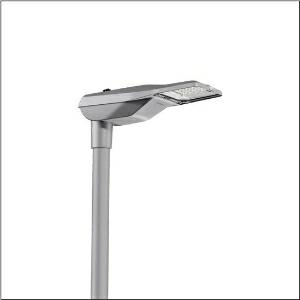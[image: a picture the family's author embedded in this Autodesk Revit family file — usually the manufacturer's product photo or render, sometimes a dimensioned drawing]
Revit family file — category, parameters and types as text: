
# Revit family: streetlight_sl_21_iq_micro___p0_5a_5xe1v31v08db_2d7c
name_source: partatom
category: Lighting Fixtures
units: mm (PartAtom-declared; Revit-internal decimal feet)

## family parameters
Cut with Voids When Loaded = No
Host = Face
Light Source = No
Part Type = Normal
Room Calculation Point = No
Round Connector Dimension = Use Diameter
Shared = No

## types (1)
- --- (1 x LED, 5030 lm, 39.1 W, 3000K)
    Apparent Load = 39 VA
    CIE Flux Codes = 37 73 96 100 100
    Color Rendering = 70
    Color Temperature = 3000K
    Default Elevation = 1800 mm
    Description = Streetlight SL 21 iQ micro, mast luminaire, primary light control with lens, of PMMA, primary optical cover: cover, of toughened safety glass, transparent, light distribution: P0.5a, light emission: direct distribution, primary light characteristic: asymmetric, installation type: post-top, side-entry, LED, High Power LED, rated luminous flux: 5.030lm, luminous efficacy: 129lm/W, light colour: 730, colour temperature: 3000K, control gear: iQ-Street Remote, D4i with power reduction, control: pre-setting: logarithmic dimming characteristic, Street-Remote, Auto-Match, Temp-Guard, Lumen-Switch, Night-Set, Smart-Wire, Light-Fading, Desk-Remote (wireless, voltage-free reading and setting of iQ features in the workshop via application-optimized NFC function/RFID function), optimised constant luminous flux control (CLO 2.0), mains connection: 220..240V, AC, 50/60Hz, start of lifetime: 39W, end of service life: 41W, reduction: 17W, luminaire housing, of diecast aluminium, powder-coated, Siteco® metallic grey (DB 702S), corrosivity category C5 mid according to DIN EN ISO 12944, please order mast flange separately, inclination adjustable: 0°, 5°, 10°, 15°, sealing non-destructively replaceable, multi-level sealing system, length: 528mm, width: 235mm, height: 110mm, mast flange for spigot size: 42mm (side-entry): 5XC10008XM4, 60/48mm (side-entry/post-top): 5XC10108XM2, 76/60mm (side-entry/post-top): 5XC10108XM1, mounting height: 4..8m, Smart Interface above, protection rating (complete): IP66, insulation class (complete): insulation class II (safety insulation), certification: CE, ENEC, ENEC+, VDE, impact resistance: IK10, permissible operating ambient temperature for outdoor applications: -40..+50°C, standard-compliant lighting for roads and squares, packaging unit: 1 piece

Light Distribution: P0.5a
    Height = 110 mm
    Lamp = 1 x LED
    Lamp Light Flux = 5030 lm
    Lamp Power = 39.1 W
    Lamp count = 1
    Length = 528 mm
    Luminous efficacy = 129 lm/W
    Manufacturer = Siteco
    ModVariant = No
    Model = 5XE1V31V08DB
    Number of Poles = 1
    OnlyDefault = Yes
    Power Factor = 1
    Product Name = Streetlight SL 21 iQ micro | P0.5a
    Product group = mast luminaire | pylon top
    ProductGroupID = 6100
    Protection Class = Protection class II
    Protection Degree = IP 66
    RLX_Detail_Level = 1
    RLX_Emergency_Light_Flux = 0 lm
    RLX_Emergency_Type = 0
    RLX_Emergency_Type_DB = No
    RlxData = <blob elided: 99001 chars, md5=f5f9927f>
    Socket = socket
    Standby Power = 0 W
    System Light Flux = 5030 lm
    System Power = 39 W
    Type Comments = factory setting: luminous flux: 100 % | dim-lin: 254 | 765 mA
    Type Image = l_1277292.jpg
    URL = http://relux.com
    VarID = @adj_070828
    Voltage = 0 V
    Weight = 0.00 kg
    Width = 235 mm

## geometry (parser evidence)
native form markers: Blend x4, Sweep x10
no freeform markers — native parametric forms only
